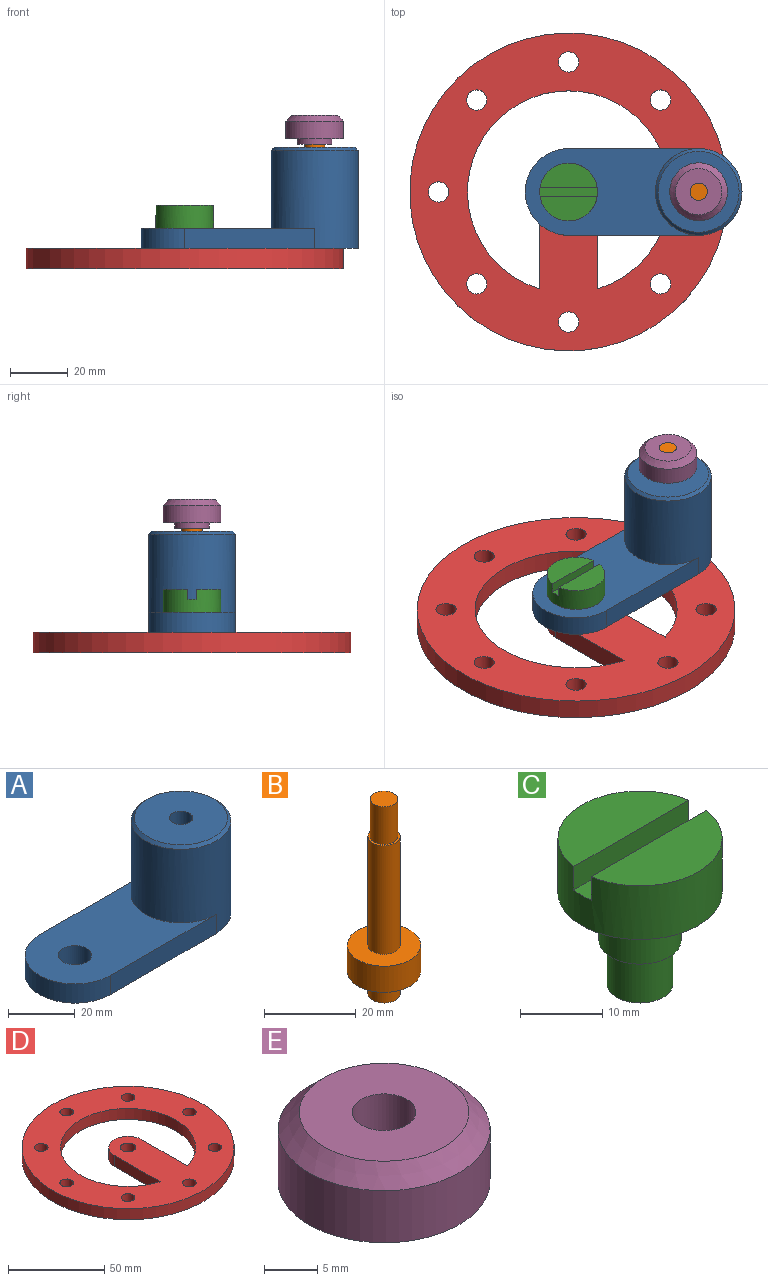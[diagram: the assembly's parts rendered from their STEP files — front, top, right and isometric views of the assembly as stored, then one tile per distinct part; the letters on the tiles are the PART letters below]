
ASSEMBLY  parts=5 mates=4
PART A: 12 faces, bbox 75x30x35 mm
  f0: plane 45x7mm, normal (0,1,0), area 315mm2, adj f1,f3,f6,f7
  f1: cylinder r=15mm len=30mm, axis (0,0,-1), area 329.9mm2, adj f0,f2,f6,f7
  f2: plane 45x7mm, normal (0,-1,0), area 315mm2, adj f1,f3,f6,f7
  f3: cylinder r=15mm len=34mm, axis (0,0,-1), area 2874.6mm2, adj f0,f2,f6,f7,f11
  f4: cylinder r=5mm len=10mm, axis (0,0,-1), area 219.9mm2, adj f6,f7
  f5: cylinder r=8.25mm len=29mm, axis (0,0,-1), area 1503.3mm2, adj f7,f8
  f6: plane 60x30mm, normal (0,0,1), area 1271.5mm2, adj f0,f1,f2,f3,f4
  f7: plane 75x30mm, normal (0,0,-1), area 1764.5mm2, adj f0,f1,f2,f3,f4,f5
  f8: plane 16.5x16.5mm, normal (0,0,-1), area 175.3mm2, adj f5,f9
  f9: cylinder r=3.5mm len=7mm, axis (0,0,-1), area 131.9mm2, adj f8,f10
  f10: plane 28x28mm, normal (0,0,1), area 577.3mm2, adj f9,f11
  f11: cone r=14mm half-angle=45deg, axis (0,0,-1), area 128.8mm2, adj f3,f10
PART B: 9 faces, bbox 16x16x52 mm
  f0: cylinder r=3.5mm len=7mm, axis (0,0,-1), area 131.9mm2, adj f1,f4
  f1: plane 7x7mm, normal (0,0,-1), area 38.5mm2, adj f0
  f2: cylinder r=8mm len=16mm, axis (0,0,-1), area 351.9mm2, adj f3,f4
  f3: plane 16x16mm, normal (0,0,1), area 162.6mm2, adj f2,f5
  f4: plane 16x16mm, normal (0,0,-1), area 162.6mm2, adj f0,f2
  f5: cylinder r=3.5mm len=29mm, axis (0,0,-1), area 637.7mm2, adj f3,f6
  f6: plane 7x7mm, normal (0,0,1), area 10.2mm2, adj f5,f7
  f7: cylinder r=3mm len=10mm, axis (0,0,-1), area 188.5mm2, adj f6,f8
  f8: plane 6x6mm, normal (0,0,1), area 28.3mm2, adj f7
PART C: 11 faces, bbox 20x20x21.7 mm
  f0: cylinder r=4mm len=8mm, axis (0,0,-1), area 163.4mm2, adj f1,f3
  f1: plane 8x8mm, normal (0,0,-1), area 50.3mm2, adj f0
  f2: cylinder r=5mm len=10mm, axis (0,0,-1), area 226.2mm2, adj f3,f6
  f3: plane 10x10mm, normal (0,0,-1), area 28.3mm2, adj f0,f2
  f4: cylinder r=10mm len=20mm, axis (0,0,-1), area 481.6mm2, adj f5,f6,f7,f8,f9,f10
  f5: plane 20x3mm, normal (0,0,1), area 59.8mm2, adj f4,f7,f9
  f6: plane 20x20mm, normal (0,0,-1), area 235.6mm2, adj f2,f4
  f7: plane 19.77x3.5mm, normal (0,-1,0), area 69.2mm2, adj f4,f5,f8
  f8: plane 19.77x8.5mm, normal (0,0,1), area 127.2mm2, adj f4,f7
  f9: plane 19.77x3.5mm, normal (0,1,0), area 69.2mm2, adj f4,f5,f10
  f10: plane 19.77x8.5mm, normal (0,0,1), area 127.2mm2, adj f4,f9
PART D: 16 faces, bbox 110x110x7 mm
  f0: cylinder r=35mm len=70mm, axis (0,0,-1), area 1397.4mm2, adj f1,f4,f14,f15
  f1: plane 33.54x7mm, normal (1,0,0), area 234.8mm2, adj f0,f2,f14,f15
  f2: cylinder r=10mm len=20mm, axis (0,0,-1), area 219.9mm2, adj f1,f4,f14,f15
  f3: cylinder r=55mm len=110mm, axis (0,0,-1), area 2419mm2, adj f14,f15
  f4: plane 33.54x7mm, normal (-1,0,0), area 234.8mm2, adj f0,f2,f14,f15
  f5: cylinder r=3.5mm len=7mm, axis (0,0,-1), area 153.9mm2, adj f14,f15
  f6: cylinder r=3.5mm len=7mm, axis (0,0,-1), area 153.9mm2, adj f14,f15
  f7: cylinder r=3.5mm len=7mm, axis (0,0,-1), area 153.9mm2, adj f14,f15
  f8: cylinder r=3.5mm len=7mm, axis (0,0,-1), area 153.9mm2, adj f14,f15
  f9: cylinder r=3.5mm len=7mm, axis (0,0,-1), area 153.9mm2, adj f14,f15
  f10: cylinder r=3.5mm len=7mm, axis (0,0,-1), area 153.9mm2, adj f14,f15
  f11: cylinder r=3.5mm len=7mm, axis (0,0,-1), area 153.9mm2, adj f14,f15
  f12: cylinder r=3.5mm len=7mm, axis (0,0,-1), area 153.9mm2, adj f14,f15
  f13: cylinder r=4mm len=8mm, axis (0,0,-1), area 175.9mm2, adj f14,f15
  f14: plane 110x110mm, normal (0,0,1), area 6144.2mm2, adj f0,f1,f2,f3,f4,f5,f6,f7
  f15: plane 110x110mm, normal (0,0,-1), area 6144.2mm2, adj f0,f1,f2,f3,f4,f5,f6,f7
PART E: 7 faces, bbox 20x20x10 mm
  f0: cylinder r=3mm len=10mm, axis (0,0,-1), area 188.5mm2, adj f2,f4
  f1: cylinder r=6mm len=12mm, axis (0,0,-1), area 75.4mm2, adj f2,f5
  f2: plane 12x12mm, normal (0,0,-1), area 84.8mm2, adj f0,f1
  f3: cylinder r=10mm len=20mm, axis (0,0,-1), area 377mm2, adj f5,f6
  f4: plane 16x16mm, normal (0,0,1), area 172.8mm2, adj f0,f6
  f5: plane 20x20mm, normal (0,0,-1), area 201.1mm2, adj f1,f3
  f6: cone r=8mm half-angle=45deg, axis (0,0,-1), area 159.9mm2, adj f3,f4
PLACE A rot(axis=(0,0,-1),0deg) t=(-16.85,-67.7,67.51)mm
PLACE B rot(axis=(0,0,-1),0deg) t=(5.65,-67.7,61.51)mm
PLACE C rot(axis=(0,0,-1),0deg) t=(-39.35,-67.7,60.81)mm
PLACE D rot(axis=(0,0,-1),0deg) t=(-39.35,-67.7,60.51)mm
PLACE E rot(axis=(0,0,-1),0deg) t=(5.65,-67.7,103.51)mm
MATE fastened E.f3 <-> B.f2  axis (0,0,-1) through (5.65,-67.7,108.51)mm
MATE parallel A.f1 <-> D.f0  axis (0,0,-1) through (-39.35,-67.7,67.51)mm
MATE slider B.f2 <-> D.f6  axis (0,0,-1) through (5.65,-67.7,67.51)mm
MATE slider C.f0 <-> A.f1  axis (0,0,-1) through (-39.35,-67.7,60.81)mm
